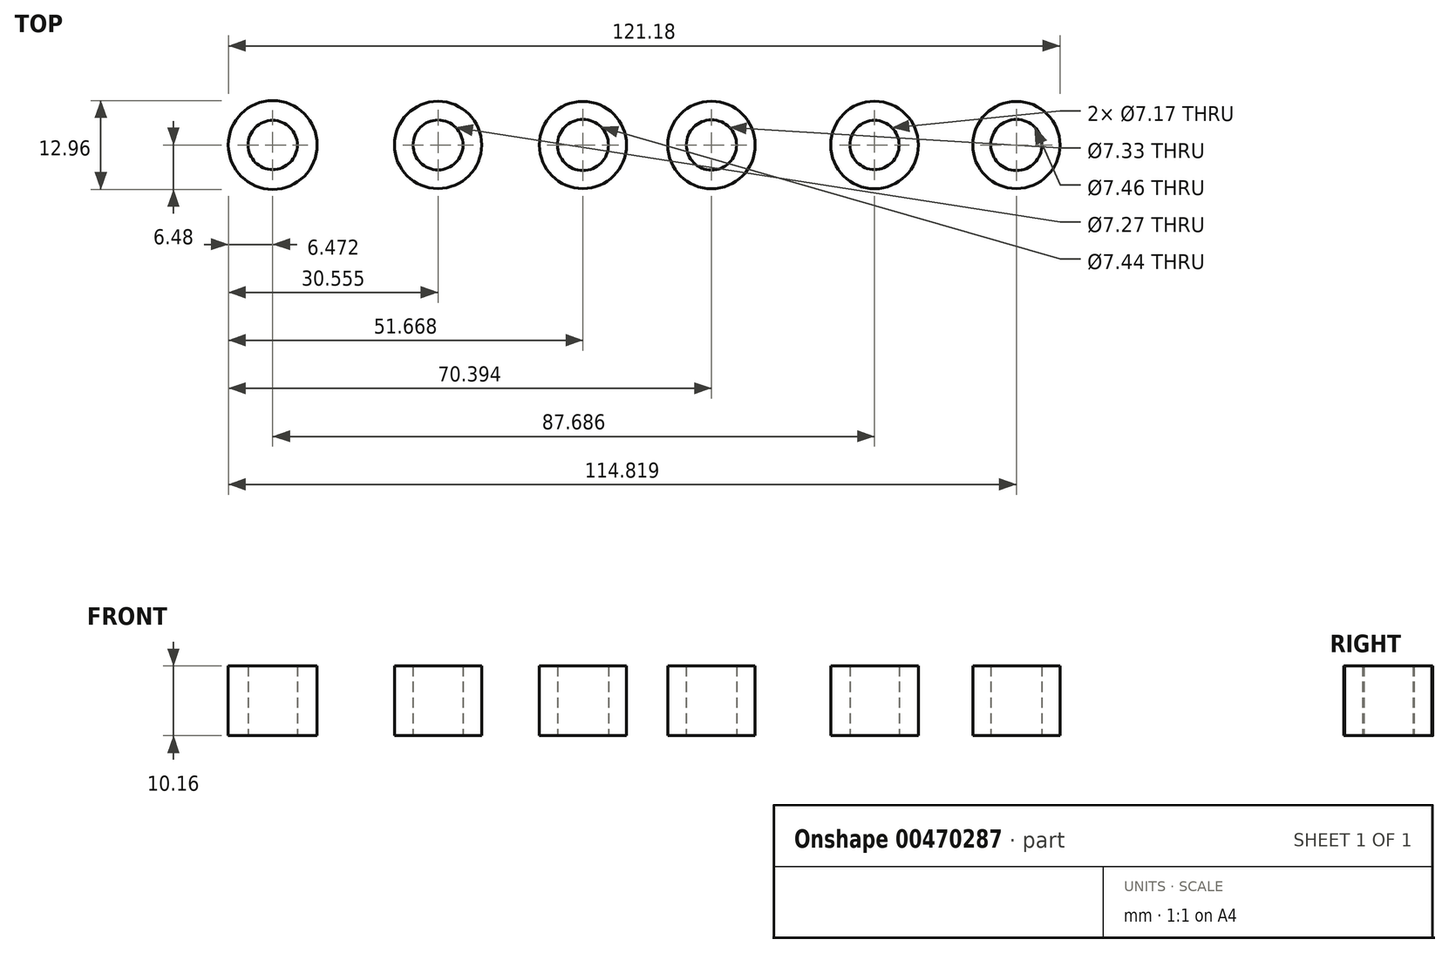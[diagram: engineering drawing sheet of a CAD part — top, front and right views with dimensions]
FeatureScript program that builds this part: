
annotation { "Feature Type Name" : "Feature", "Feature Type Description" : "" }
export const myFeature = defineFeature(function(context is Context, id is Id, definition is map)
    precondition{}
    {
        {
            var Q0;
            Q0=qCreatedBy(makeId("Top.planeOp"),FACE);
            var sketch = newSketch(context, id + "F0", { "sketchPlane" : qUnion([Q0])});
            skCircle(sketch, "E0", {"center": v(-12.63, 0) * mm, "radius": 6.35 * mm});
            skCircle(sketch, "E1", {"center": v(-33.75, 0) * mm, "radius": 6.36 * mm});
            skCircle(sketch, "E2", {"center": v(-57.83, 0) * mm, "radius": 6.48 * mm});
            skCircle(sketch, "E3", {"center": v(-12.63, 0) * mm, "radius": 3.72 * mm});
            skCircle(sketch, "E4", {"center": v(-33.75, 0) * mm, "radius": 3.63 * mm});
            skCircle(sketch, "E5", {"center": v(-57.83, 0) * mm, "radius": 3.59 * mm});
            skSolve(sketch);
        }
        {
            var Q0;
            Q0=makeQuery(id+"F0.imprint","IMPRINT",FACE,{"disambiguationData":[TD([[makeQuery(id+"F0.imprint","IMPRINT",EDGE,{"derivedFrom":sQuery(id+"F0.wireOp",EDGE,"E0")}),1.0]])]});
            var Q1;
            Q1=makeQuery(id+"F0.imprint","IMPRINT",FACE,{"disambiguationData":[TD([[makeQuery(id+"F0.imprint","IMPRINT",EDGE,{"derivedFrom":sQuery(id+"F0.wireOp",EDGE,"E1")}),1.0]])]});
            var Q2;
            Q2=makeQuery(id+"F0.imprint","IMPRINT",FACE,{"disambiguationData":[TD([[makeQuery(id+"F0.imprint","IMPRINT",EDGE,{"derivedFrom":sQuery(id+"F0.wireOp",EDGE,"E2")}),1.0]])]});
            extrude(context, id + "F1", {"entities" : qUnion([Q0, Q1, Q2]), "depth" : 10.16 * mm});
        }
        {
            var Q0;
            Q0=qCreatedBy(makeId("Top.planeOp"),FACE);
            var sketch = newSketch(context, id + "F2", { "sketchPlane" : qUnion([Q0])});
            skPoint(sketch, "E6", {"position": v(6.1, 0) * mm});
            skCircle(sketch, "E7", {"center": v(6.1, 0) * mm, "radius": 6.38 * mm});
            skCircle(sketch, "E8", {"center": v(6.1, 0) * mm, "radius": 3.67 * mm});
            skCircle(sketch, "E9", {"center": v(29.86, 0) * mm, "radius": 6.38 * mm});
            skCircle(sketch, "E10", {"center": v(29.86, 0) * mm, "radius": 3.59 * mm});
            skCircle(sketch, "E11", {"center": v(50.52, 0) * mm, "radius": 6.36 * mm});
            skCircle(sketch, "E12", {"center": v(50.52, 0) * mm, "radius": 3.73 * mm});
            skSolve(sketch);
        }
        {
            var Q0;
            Q0=makeQuery(id+"F2.imprint","IMPRINT",FACE,{"disambiguationData":[TD([[makeQuery(id+"F2.imprint","IMPRINT",EDGE,{"derivedFrom":sQuery(id+"F2.wireOp",EDGE,"tJlllPaZ-rPJG-gJ3N-yyJd-Wehy86mZBwW7")}),1.0]])]});
            var Q1;
            Q1=makeQuery(id+"F2.imprint","IMPRINT",FACE,{"disambiguationData":[TD([[makeQuery(id+"F2.imprint","IMPRINT",EDGE,{"derivedFrom":sQuery(id+"F2.wireOp",EDGE,"G7YVFECH-lxMh-ON9n-eOyq-p3n3YfgBWKJM")}),-1.0]])]});
            var Q2;
            Q2=makeQuery(id+"F2.imprint","IMPRINT",FACE,{"disambiguationData":[TD([[makeQuery(id+"F2.imprint","IMPRINT",EDGE,{"derivedFrom":sQuery(id+"F2.wireOp",EDGE,"85CdOqKE-BHkA-t1eM-xv5T-WUhNmOm1G8Vw")}),-1.0]])]});
            var Q3;
            Q3=makeQuery(id+"F2.imprint","IMPRINT",FACE,{"disambiguationData":[TD([[makeQuery(id+"F2.imprint","IMPRINT",EDGE,{"derivedFrom":sQuery(id+"F2.wireOp",EDGE,"E11")}),1.0]])]});
            var Q4;
            {var subQ2=sQuery(id+"F2.wireOp",EDGE,"nmH1gZNE-B3ry-L4wz-N9wX-kNXvy8hFpg3r");var subQ4=sQuery(id+"F2.wireOp",EDGE,"E7");var subQ5=makeQuery(id+"F2.imprint","INTERSECT",VERTEX,{"disambiguationData":[OD(0.0)],"derivedFrom":[subQ4,subQ2]});Q4=makeQuery(id+"F2.imprint","IMPRINT",FACE,{"disambiguationData":[TD([[makeQuery(id+"F2.imprint","IMPRINT",EDGE,{"disambiguationData":[TD([[subQ5,1.0]])],"derivedFrom":subQ4}),1.0]])]});}
            var Q5;
            Q5=makeQuery(id+"F2.imprint","IMPRINT",FACE,{"disambiguationData":[TD([[makeQuery(id+"F2.imprint","IMPRINT",EDGE,{"derivedFrom":sQuery(id+"F2.wireOp",EDGE,"E7")}),1.0]])]});
            var Q6;
            Q6=makeQuery(id+"F2.imprint","IMPRINT",FACE,{"disambiguationData":[TD([[makeQuery(id+"F2.imprint","IMPRINT",EDGE,{"derivedFrom":sQuery(id+"F2.wireOp",EDGE,"E9")}),1.0]])]});
            extrude(context, id + "F3", {"entities" : qUnion([Q0, Q1, Q2, Q3, Q4, Q5, Q6]), "depth" : 10.16 * mm});
        }
    });
